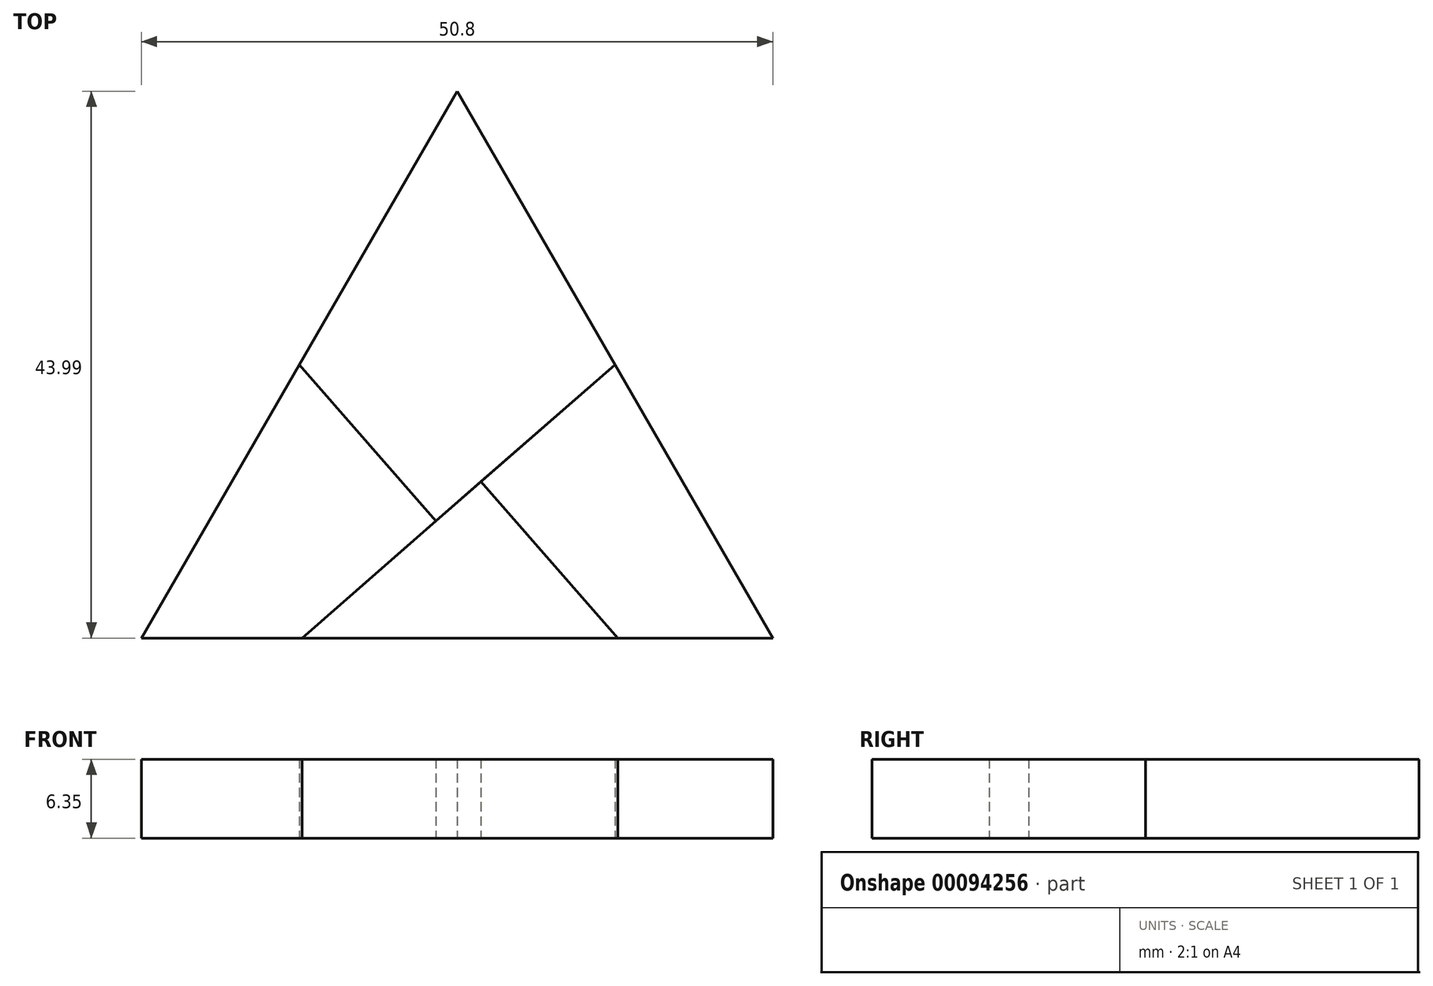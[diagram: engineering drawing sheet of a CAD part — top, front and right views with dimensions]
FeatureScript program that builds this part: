
annotation { "Feature Type Name" : "Feature", "Feature Type Description" : "" }
export const myFeature = defineFeature(function(context is Context, id is Id, definition is map)
    precondition{}
    {
        {
            var Q0;
            Q0=qCreatedBy(makeId("Top.planeOp"),FACE);
            var sketch = newSketch(context, id + "F0", { "sketchPlane" : qUnion([Q0])});
            skLineSegment(sketch, "E0", {"start": v(-50.8, 0) * mm, "end": v(-25.4, 44) * mm});
            skLineSegment(sketch, "E1", {"start": v(-50.8, 0) * mm, "end": v(0, 0) * mm});
            skLineSegment(sketch, "E2", {"start": v(0, 0) * mm, "end": v(-25.4, 44) * mm});
            skLineSegment(sketch, "E3", {"start": v(-12.7, 22) * mm, "end": v(-37.87, 0) * mm});
            skLineSegment(sketch, "E4", {"start": v(-38.1, 22) * mm, "end": v(-27.1, 9.41) * mm});
            skLineSegment(sketch, "E5", {"start": v(-23.47, 12.59) * mm, "end": v(-12.47, 0) * mm});
            skLineSegment(sketch, "E6", {"start": v(-37.87, 0) * mm, "end": v(-12.47, 0) * mm});
            skLineSegment(sketch, "E7", {"start": v(0, 0) * mm, "end": v(0, 33.43) * mm});
            skLineSegment(sketch, "E8.bottom", {"start": v(0, 0) * mm, "end": v(33.43, 0) * mm});
            skLineSegment(sketch, "E8.top", {"start": v(0, 33.43) * mm, "end": v(33.43, 33.43) * mm});
            skLineSegment(sketch, "E8.right", {"start": v(33.43, 0) * mm, "end": v(33.43, 33.43) * mm});
            skLineSegment(sketch, "E9", {"start": v(-23.47, 12.59) * mm, "end": v(-12.7, 22) * mm});
            skLineSegment(sketch, "E10", {"start": v(-23.47, 12.59) * mm, "end": v(-27.1, 9.41) * mm});
            skLineSegment(sketch, "E11", {"start": v(-27.1, 9.41) * mm, "end": v(-37.87, 0) * mm});
            skLineSegment(sketch, "E12", {"start": v(0, 18.83) * mm, "end": v(0, 33.43) * mm});
            skLineSegment(sketch, "E13", {"start": v(0, 0) * mm, "end": v(0, 18.83) * mm});
            skLineSegment(sketch, "E14", {"start": v(33.43, 33.43) * mm, "end": v(33.43, 28.58) * mm});
            skLineSegment(sketch, "E15", {"start": v(33.43, 28.58) * mm, "end": v(33.43, 0) * mm});
            skLineSegment(sketch, "E16", {"start": v(0, -27) * mm, "end": v(26.47, -27) * mm});
            skLineSegment(sketch, "E17", {"start": v(26.47, -27) * mm, "end": v(33.43, -27) * mm});
            skLineSegment(sketch, "E18", {"start": v(0, -44.63) * mm, "end": v(16.71, -44.63) * mm});
            skLineSegment(sketch, "E19", {"start": v(16.71, -44.63) * mm, "end": v(33.43, -44.63) * mm});
            skSolve(sketch);
        }
        {
            var Q0;
            {var subQ3=sQuery(id+"F0.wireOp",EDGE,"E4");Q0=makeQuery(id+"F0.imprint","IMPRINT",FACE,{"disambiguationData":[TD([[makeQuery(id+"F0.imprint","IMPRINT",EDGE,{"derivedFrom":subQ3}),-1.0]])]});}
            var Q1;
            {var subQ3=sQuery(id+"F0.wireOp",EDGE,"E5");Q1=makeQuery(id+"F0.imprint","IMPRINT",FACE,{"disambiguationData":[TD([[makeQuery(id+"F0.imprint","IMPRINT",EDGE,{"derivedFrom":subQ3}),1.0]])]});}
            extrude(context, id + "F1", {"entities" : qUnion([Q0, Q1]), "depth" : 6.35 * mm});
        }
        {
            var Q0;
            {var subQ1=sQuery(id+"F0.wireOp",EDGE,"E4");Q0=makeQuery(id+"F0.imprint","IMPRINT",FACE,{"disambiguationData":[TD([[makeQuery(id+"F0.imprint","IMPRINT",EDGE,{"derivedFrom":subQ1}),1.0]])]});}
            extrude(context, id + "F3", {"entities" : qUnion([Q0]), "depth" : 6.35 * mm});
        }
        {
            var Q0;
            Q0=makeQuery(id+"F0.imprint","IMPRINT",FACE,{"disambiguationData":[TD([[makeQuery(id+"F0.imprint","IMPRINT",EDGE,{"derivedFrom":sQuery(id+"F0.wireOp",EDGE,"E5")}),-1.0]])]});
            extrude(context, id + "F2", {"entities" : qUnion([Q0]), "depth" : 6.35 * mm});
        }
    });
